# Revit family: led_e_c_module_22w_dim_2700k_clio_ct_140066204
name_source: partatom
category: Leuchten
revit_build: Autodesk Revit 2016 (Build: 20190508_0715(x64)
units: mm (PartAtom-declared; Revit-internal decimal feet)

## family parameters
Basisbauteil = Fläche
Beim Laden mit Abzugskörper schneiden = Nein
Bemaßung runder Anschluss = Durchmesser verwenden
Gemeinsam genutzt = Nein
Lichtquelle = Nein
Raumberechnungspunkt = Nein
Teiletyp = Normal

## types (1)
- LED E C module 22W DIM 2700K Clio CT (1 x LED, 2300 lm)
    Approval mark = CE
    Beschreibung = Fits well in slim ceiling luminaires. Easy and flexible installation. Shadow free, homogeneous light diffusion. Integrated driver. Including magnets and connection box. Daylight and motion sensor accessory available.
    CIE Flux Codes = 28 60 90 95 100
    Height = 29 mm
    Hersteller = OPPLE
    Lamp Light Flux = 2300 lm
    Lamp count = 1
    Lampe = 1 x LED
    Length = 228 mm
    Luminous efficacy = 105 lm/W
    ModVariant = Nein
    Modell = 140066204
    Mounting Place = Ceiling, Wall
    Mounting Type = Surface mounted
    Number of Poles = 1
    OnlyDefault = Ja
    Power Factor = 1
    Product Name = LED E C module 22W DIM 2700K Clio CT
    Product group = Module Clio G2
    ProductGroupID = 315
    Protection Class = Protection class I
    Protection Degree = IP 20
    RLX_Detail_Level = 1
    RlxData = <blob elided: 25153 chars, md5=8a61819e>
    Scheinlast = 22 VA
    Socket = socket
    Standby Power = 0 W
    System Light Flux = 2305 lm
    System Power = 22 W
    Typenbild = 140066204.jpg
    Typenkommentare = Product without accessories
    URL = http://relux.com
    VarID = ---
    Voltage = 0 V
    Vorgabe-Ansicht = 1800 mm
    Weight = 0.00 kg
    Width = 0 mm  [stored 0 ft]

note: [stored X ft] marks values corroborated as IEEE doubles in the binary element streams (Revit-internal decimal feet)

## geometry (parser evidence)
native form markers: Blend x4, Sweep x9
no freeform markers — native parametric forms only
